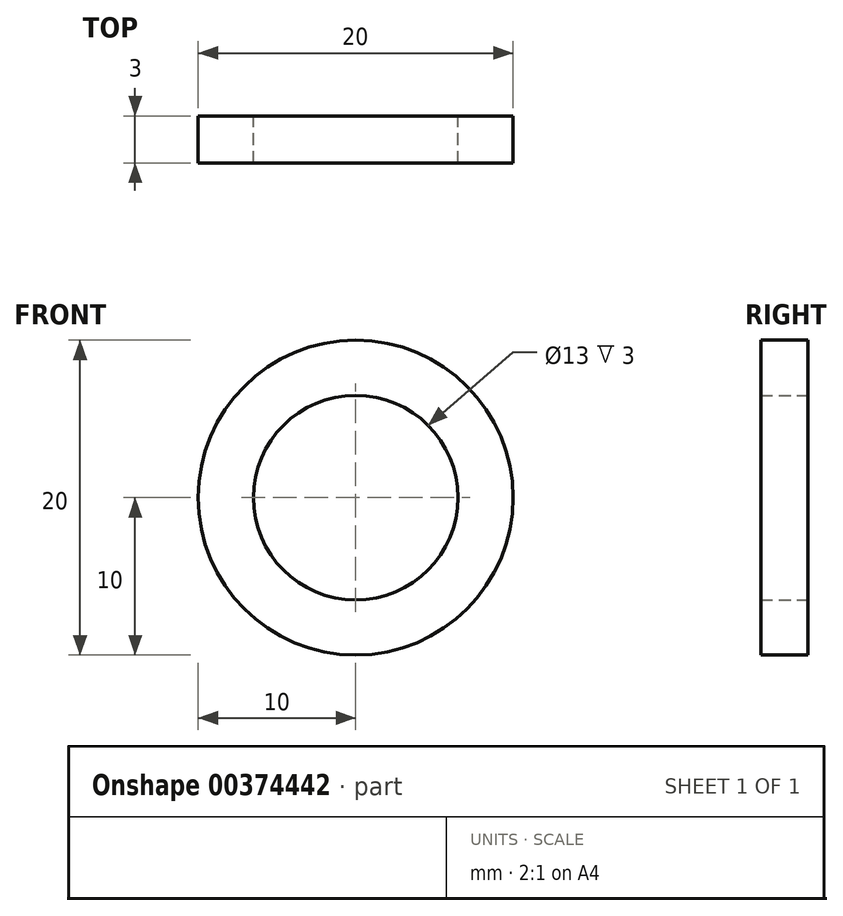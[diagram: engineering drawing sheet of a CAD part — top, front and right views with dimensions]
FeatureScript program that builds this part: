
annotation { "Feature Type Name" : "Feature", "Feature Type Description" : "" }
export const myFeature = defineFeature(function(context is Context, id is Id, definition is map)
    precondition{}
    {
        {
            var Q0;
            Q0=qCreatedBy(makeId("Front.planeOp"),FACE);
            var sketch = newSketch(context, id + "F0", { "sketchPlane" : qUnion([Q0])});
            skCircle(sketch, "E0", {"center": v(0, 0) * mm, "radius": 6.5 * mm});
            skCircle(sketch, "E1", {"center": v(0, 0) * mm, "radius": 10 * mm});
            skSolve(sketch);
        }
        {
            var Q0;
            Q0 = qSketchRegion(id + "F0", true);
            extrude(context, id + "F1", {"entities" : qUnion([Q0]), "depth" : 3 * mm});
        }
    });
